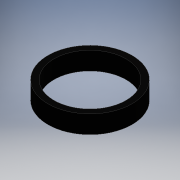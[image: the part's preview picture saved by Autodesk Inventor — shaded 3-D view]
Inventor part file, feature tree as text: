
AUTODESK INVENTOR PART (.ipt)
format: ipt  version: 2016 (Build 200138000, 138)  size: 95,744 bytes
history: native  units: mm
features: other x1, extrude x1, sketch x1
ambient origin geometry x8: Origin, YZ Plane, XZ Plane, XY Plane, X Axis, Y Axis, Z Axis, Center Point
bodies: Body1 (feature_tree)
feature tree (3):
  other  "ソリッド1"
  extrude  "押し出し1"  Depth=14.0mm
  sketch  "スケッチ1"
